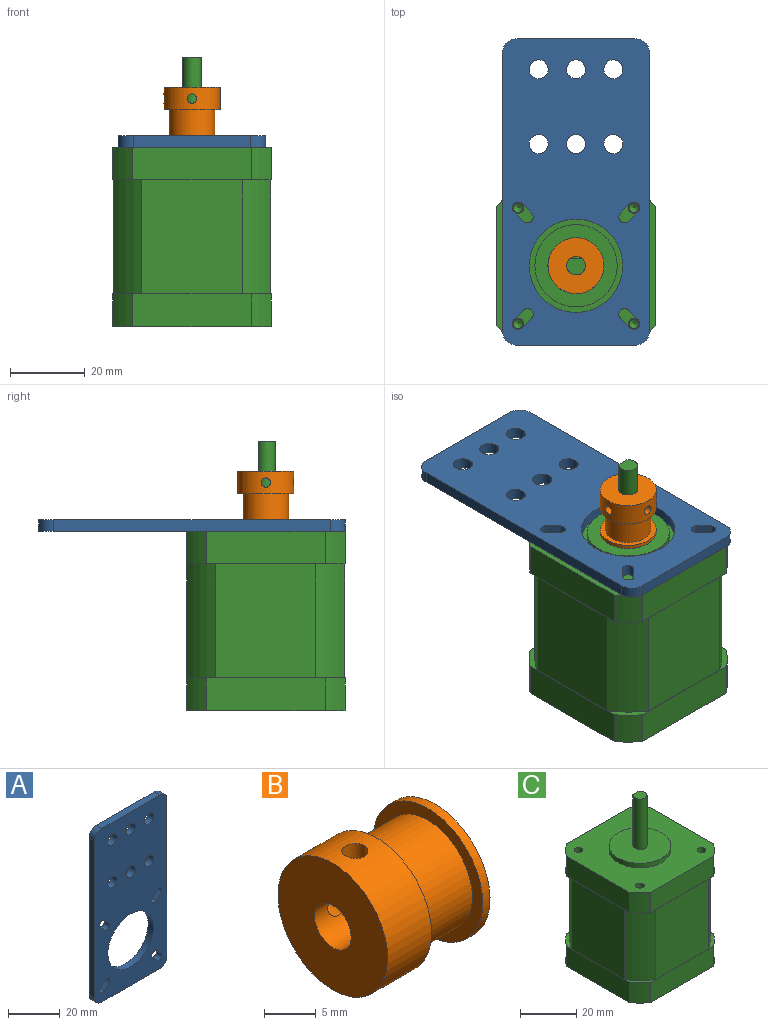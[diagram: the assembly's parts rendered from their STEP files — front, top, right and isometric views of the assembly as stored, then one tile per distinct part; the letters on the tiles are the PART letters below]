
ASSEMBLY  parts=3 mates=2
PART A: 33 faces, bbox 39.5x3x82 mm
  f0: plane 82x39.5mm, normal (0,1,0), area 2537.8mm2, adj f2,f3,f4,f5,f6,f7,f8,f9
  f1: plane 82x39.5mm, normal (0,-1,0), area 2537.8mm2, adj f2,f3,f4,f5,f6,f7,f8,f9
  f2: cylinder r=4mm len=4mm, axis (0,-1,0), area 18.8mm2, adj f0,f1,f3,f9
  f3: plane 31.5x3mm, normal (0,0,1), area 94.5mm2, adj f0,f1,f2,f4
  f4: cylinder r=4mm len=4mm, axis (0,-1,0), area 18.8mm2, adj f0,f1,f3,f5
  f5: plane 74x3mm, normal (1,0,0), area 222mm2, adj f0,f1,f4,f6
  f6: cylinder r=4mm len=4mm, axis (0,-1,0), area 18.8mm2, adj f0,f1,f5,f7
  f7: plane 31.5x3mm, normal (0,0,-1), area 94.5mm2, adj f0,f1,f6,f8
  f8: cylinder r=4mm len=4mm, axis (0,-1,0), area 18.8mm2, adj f0,f1,f7,f9
  f9: plane 74x3mm, normal (-1,0,0), area 222mm2, adj f0,f1,f2,f8
  f10: cylinder r=12.5mm len=25mm, axis (0,-1,0), area 235.6mm2, adj f0,f1
  f11: cylinder r=1.55mm len=3mm, axis (0,-1,0), area 14.6mm2, adj f0,f1,f12,f14
  f12: plane 3x2.5mm, normal (-0.71,0,-0.71), area 10.6mm2, adj f0,f1,f11,f13
  f13: cylinder r=1.55mm len=3mm, axis (0,-1,0), area 14.6mm2, adj f0,f1,f12,f14
  f14: plane 3x2.5mm, normal (0.71,0,0.71), area 10.6mm2, adj f0,f1,f11,f13
  f15: cylinder r=2.55mm len=5.1mm, axis (0,-1,0), area 48.1mm2, adj f0,f1
  f16: cylinder r=2.55mm len=5.1mm, axis (0,-1,0), area 48.1mm2, adj f0,f1
  f17: cylinder r=2.55mm len=5.1mm, axis (0,-1,0), area 48.1mm2, adj f0,f1
  f18: cylinder r=2.55mm len=5.1mm, axis (0,-1,0), area 48.1mm2, adj f0,f1
  f19: cylinder r=2.55mm len=5.1mm, axis (0,-1,0), area 48.1mm2, adj f0,f1
  f20: cylinder r=2.55mm len=5.1mm, axis (0,-1,0), area 48.1mm2, adj f0,f1
  f21: cylinder r=1.55mm len=3mm, axis (0,-1,0), area 14.6mm2, adj f0,f1,f22,f24
  f22: plane 3x2.5mm, normal (-0.71,0,0.71), area 10.6mm2, adj f0,f1,f21,f23
  f23: cylinder r=1.55mm len=3mm, axis (0,-1,0), area 14.6mm2, adj f0,f1,f22,f24
  f24: plane 3x2.5mm, normal (0.71,0,-0.71), area 10.6mm2, adj f0,f1,f21,f23
  f25: cylinder r=1.55mm len=3mm, axis (0,-1,0), area 14.6mm2, adj f0,f1,f26,f28
  f26: plane 3x2.5mm, normal (0.71,0,0.71), area 10.6mm2, adj f0,f1,f25,f27
  f27: cylinder r=1.55mm len=3mm, axis (0,-1,0), area 14.6mm2, adj f0,f1,f26,f28
  f28: plane 3x2.5mm, normal (-0.71,0,-0.71), area 10.6mm2, adj f0,f1,f25,f27
  f29: cylinder r=1.55mm len=3mm, axis (0,-1,0), area 14.6mm2, adj f0,f1,f30,f32
  f30: plane 3x2.5mm, normal (0.71,0,-0.71), area 10.6mm2, adj f0,f1,f29,f31
  f31: cylinder r=1.55mm len=3mm, axis (0,-1,0), area 14.6mm2, adj f0,f1,f30,f32
  f32: plane 3x2.5mm, normal (-0.71,0,0.71), area 10.6mm2, adj f0,f1,f29,f31
PART B: 10 faces, bbox 14x15x15 mm
  f0: cylinder r=2.5mm len=14mm, axis (1,0,0), area 209.8mm2, adj f1,f7,f8,f9
  f1: plane 15x15mm, normal (-1,0,0), area 157.1mm2, adj f0,f2
  f2: cylinder r=7.5mm len=15mm, axis (1,0,0), area 272.9mm2, adj f1,f3,f8,f9
  f3: plane 15x15mm, normal (1,0,0), area 59.8mm2, adj f2,f4
  f4: cylinder r=6.1mm len=12.2mm, axis (1,0,0), area 268.3mm2, adj f3,f5
  f5: plane 15x15mm, normal (-1,0,0), area 59.8mm2, adj f4,f6
  f6: cylinder r=7.5mm len=15mm, axis (1,0,0), area 47.1mm2, adj f5,f7
  f7: plane 15x15mm, normal (1,0,0), area 157.1mm2, adj f0,f6
  f8: cylinder r=1.25mm len=5.34mm, axis (0,-1,0), area 40.2mm2, adj f0,f2
  f9: cylinder r=1.25mm len=5.34mm, axis (0,0,-1), area 40.2mm2, adj f0,f2
PART C: 50 faces, bbox 42.4x42.4x72 mm
  f0: cylinder r=2.5mm len=22mm, axis (0,0,-1), area 297.3mm2, adj f1,f2,f29,f30
  f1: plane 5x4.5mm, normal (0,0,1), area 18.6mm2, adj f0,f29
  f2: plane 22x22mm, normal (0,0,1), area 360.5mm2, adj f0,f3
  f3: cylinder r=11mm len=22mm, axis (0,0,-1), area 138.2mm2, adj f2,f8
  f4: plane 31.78x8.75mm, normal (1,0,0), area 278mm2, adj f8,f9,f10,f32
  f5: plane 31.78x8.75mm, normal (0,-1,0), area 278mm2, adj f8,f9,f11,f32
  f6: plane 31.78x8.75mm, normal (-1,0,0), area 278mm2, adj f8,f11,f12,f32
  f7: plane 31.78x8.75mm, normal (0,1,0), area 278mm2, adj f8,f10,f12,f32
  f8: plane 42.42x42.42mm, normal (0,0,1), area 1339.6mm2, adj f3,f4,f5,f6,f7,f9,f10,f11
  f9: cylinder r=26.5mm len=8.75mm, axis (0,0,-1), area 66.1mm2, adj f4,f5,f8,f32
  f10: cylinder r=26.5mm len=8.75mm, axis (0,0,-1), area 66.1mm2, adj f4,f7,f8,f32
  f11: cylinder r=26.5mm len=8.75mm, axis (0,0,-1), area 66.1mm2, adj f5,f6,f8,f32
  f12: cylinder r=26.5mm len=8.75mm, axis (0,0,-1), area 66.1mm2, adj f6,f7,f8,f32
  f13: cone r=1.25mm half-angle=59deg, axis (0,0,1), area 5.7mm2, adj f14
  f14: cylinder r=1.25mm len=2.5mm, axis (0,0,1), area 11.8mm2, adj f13,f15
  f15: plane 3x3mm, normal (0,0,1), area 2.2mm2, adj f14,f16
  f16: cylinder r=1.5mm len=6mm, axis (0,0,1), area 56.5mm2, adj f8,f15
  f17: cone r=1.25mm half-angle=59deg, axis (0,0,1), area 5.7mm2, adj f18
  f18: cylinder r=1.25mm len=2.5mm, axis (0,0,1), area 11.8mm2, adj f17,f19
  f19: plane 3x3mm, normal (0,0,1), area 2.2mm2, adj f18,f20
  f20: cylinder r=1.5mm len=6mm, axis (0,0,1), area 56.5mm2, adj f8,f19
  f21: cone r=1.25mm half-angle=59deg, axis (0,0,1), area 5.7mm2, adj f22
  f22: cylinder r=1.25mm len=2.5mm, axis (0,0,1), area 11.8mm2, adj f21,f23
  f23: plane 3x3mm, normal (0,0,1), area 2.2mm2, adj f22,f24
  f24: cylinder r=1.5mm len=6mm, axis (0,0,1), area 56.5mm2, adj f8,f23
  f25: cone r=1.25mm half-angle=59deg, axis (0,0,1), area 5.7mm2, adj f26
  f26: cylinder r=1.25mm len=2.5mm, axis (0,0,1), area 11.8mm2, adj f25,f27
  f27: plane 3x3mm, normal (0,0,1), area 2.2mm2, adj f26,f28
  f28: cylinder r=1.5mm len=6mm, axis (0,0,1), area 56.5mm2, adj f8,f27
  f29: plane 15x3mm, normal (0,1,0), area 45mm2, adj f0,f1,f30
  f30: plane 3x0.5mm, normal (0,0,1), area 1mm2, adj f0,f29
  f31: plane 42.42x42.42mm, normal (0,0,1), area 67.2mm2, adj f33,f34,f35,f36,f37,f38,f39,f40
  f32: plane 42.42x42.42mm, normal (0,0,-1), area 67.2mm2, adj f4,f5,f6,f7,f9,f10,f11,f12
  f33: cylinder r=25mm len=30.5mm, axis (0,0,1), area 335.5mm2, adj f31,f32,f34,f40
  f34: plane 30.5x26.79mm, normal (0,1,0), area 817.1mm2, adj f31,f32,f33,f35
  f35: cylinder r=25mm len=30.5mm, axis (0,0,1), area 335.5mm2, adj f31,f32,f34,f36
  f36: plane 30.5x26.79mm, normal (1,0,0), area 817.1mm2, adj f31,f32,f35,f37
  f37: cylinder r=25mm len=30.5mm, axis (0,0,1), area 335.5mm2, adj f31,f32,f36,f38
  f38: plane 30.5x26.79mm, normal (0,-1,0), area 817.1mm2, adj f31,f32,f37,f39
  f39: cylinder r=25mm len=30.5mm, axis (0,0,1), area 335.5mm2, adj f31,f32,f38,f40
  f40: plane 30.5x26.79mm, normal (-1,0,0), area 817.1mm2, adj f31,f32,f33,f39
  f41: plane 42.42x42.42mm, normal (0,0,-1), area 1748.1mm2, adj f42,f43,f44,f45,f46,f47,f48,f49
  f42: cylinder r=26.5mm len=8.75mm, axis (0,0,-1), area 66.1mm2, adj f31,f41,f48,f49
  f43: cylinder r=26.5mm len=8.75mm, axis (0,0,-1), area 66.1mm2, adj f31,f41,f47,f48
  f44: cylinder r=26.5mm len=8.75mm, axis (0,0,-1), area 66.1mm2, adj f31,f41,f46,f47
  f45: cylinder r=26.5mm len=8.75mm, axis (0,0,-1), area 66.1mm2, adj f31,f41,f46,f49
  f46: plane 31.78x8.75mm, normal (0,1,0), area 278mm2, adj f31,f41,f44,f45
  f47: plane 31.78x8.75mm, normal (-1,0,0), area 278mm2, adj f31,f41,f43,f44
  f48: plane 31.78x8.75mm, normal (0,-1,0), area 278mm2, adj f31,f41,f42,f43
  f49: plane 31.78x8.75mm, normal (1,0,0), area 278mm2, adj f31,f41,f42,f45
PLACE A rot(axis=(-1,0,0),90deg) t=(-1.98,-10.05,1.64)mm
PLACE B rot(axis=(0.71,0,-0.71),180deg) t=(-1.98,-10.05,14.64)mm
PLACE C t=(-1.98,-10.05,-1.36)mm
MATE fastened A.f10 <-> C.f0  axis (0,0,-1) through (-1.98,-10.05,-1.36)mm
MATE fastened B.f0 <-> A.f10  axis (0,0,1) through (-1.98,-10.05,1.64)mm
